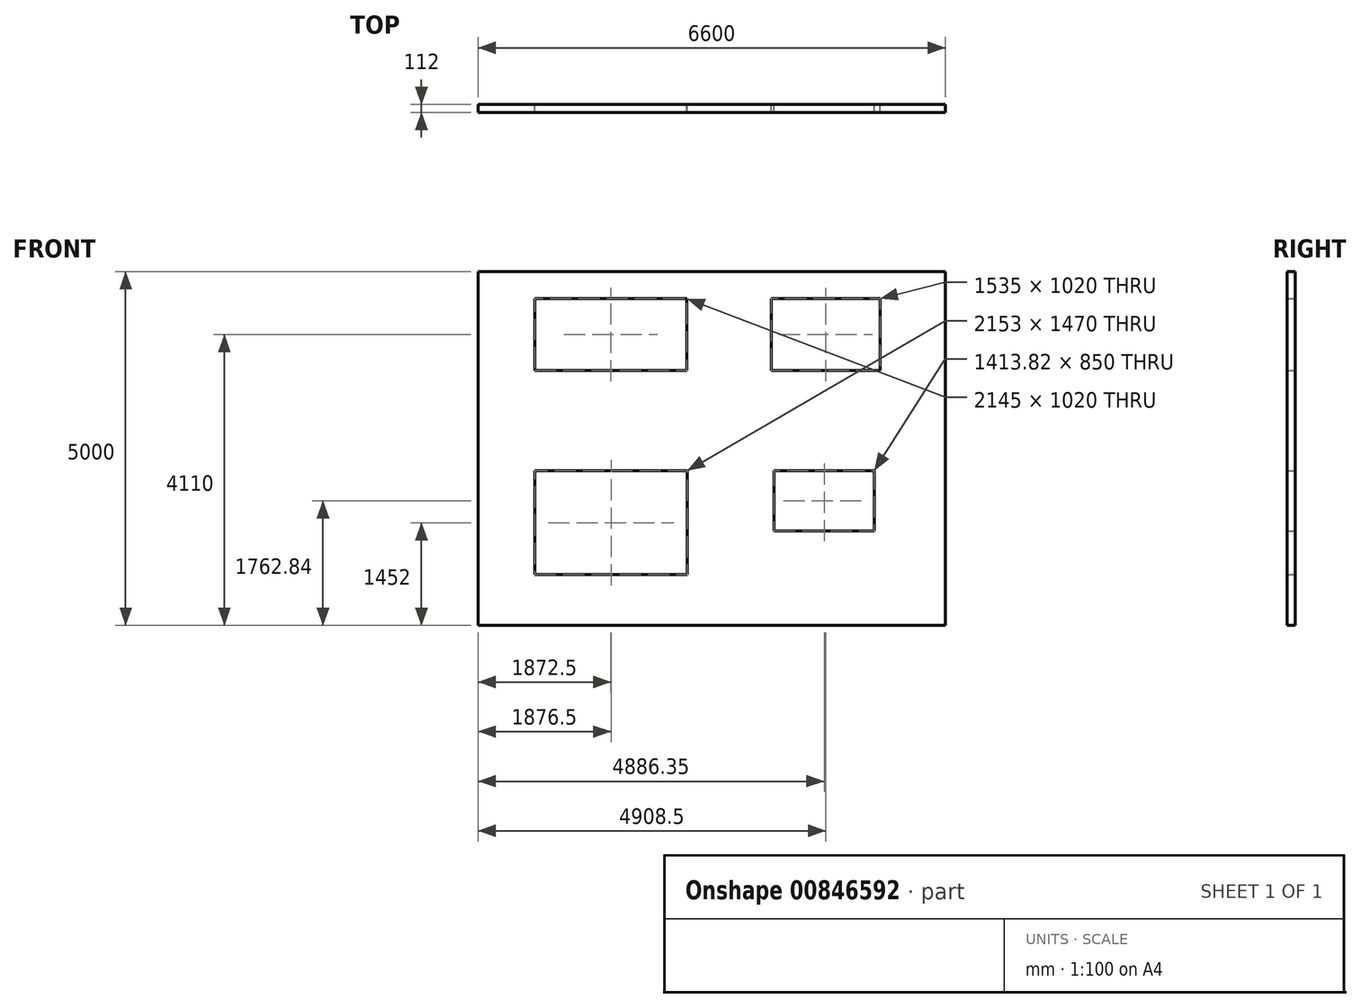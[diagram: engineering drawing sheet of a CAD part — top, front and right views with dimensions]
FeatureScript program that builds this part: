
annotation { "Feature Type Name" : "Feature", "Feature Type Description" : "" }
export const myFeature = defineFeature(function(context is Context, id is Id, definition is map)
    precondition{}
    {
        {
            var Q0;
            Q0=qCreatedBy(makeId("Front.planeOp"),FACE);
            var sketch = newSketch(context, id + "F0", { "sketchPlane" : qUnion([Q0])});
            skLineSegment(sketch, "E0.bottom", {"start": v(3288.8, -2773.48) * mm, "end": v(-3311.2, -2773.48) * mm});
            skLineSegment(sketch, "E0.top", {"start": v(3288.8, 2226.52) * mm, "end": v(-3311.2, 2226.52) * mm});
            skLineSegment(sketch, "E0.left", {"start": v(3288.8, -2773.48) * mm, "end": v(3288.8, 2226.52) * mm});
            skLineSegment(sketch, "E0.right", {"start": v(-3311.2, -2773.48) * mm, "end": v(-3311.2, 2226.52) * mm});
            skLineSegment(sketch, "E1.bottom", {"start": v(-2511.2, 1846.52) * mm, "end": v(-366.2, 1846.52) * mm});
            skLineSegment(sketch, "E1.top", {"start": v(-2511.2, 826.52) * mm, "end": v(-366.2, 826.52) * mm});
            skLineSegment(sketch, "E1.left", {"start": v(-2511.2, 1846.52) * mm, "end": v(-2511.2, 826.52) * mm});
            skLineSegment(sketch, "E1.right", {"start": v(-366.2, 1846.52) * mm, "end": v(-366.2, 826.52) * mm});
            skLineSegment(sketch, "E2.bottom", {"start": v(2364.8, 1846.52) * mm, "end": v(829.8, 1846.52) * mm});
            skLineSegment(sketch, "E2.top", {"start": v(2364.8, 826.52) * mm, "end": v(829.8, 826.52) * mm});
            skLineSegment(sketch, "E2.left", {"start": v(2364.8, 1846.52) * mm, "end": v(2364.8, 826.52) * mm});
            skLineSegment(sketch, "E2.right", {"start": v(829.8, 1846.52) * mm, "end": v(829.8, 826.52) * mm});
            skLineSegment(sketch, "E3.bottom", {"start": v(-2511.2, -2056.48) * mm, "end": v(-358.2, -2056.48) * mm});
            skLineSegment(sketch, "E3.top", {"start": v(-2511.2, -586.48) * mm, "end": v(-358.2, -586.48) * mm});
            skLineSegment(sketch, "E3.left", {"start": v(-2511.2, -2056.48) * mm, "end": v(-2511.2, -586.48) * mm});
            skLineSegment(sketch, "E3.right", {"start": v(-358.2, -2056.48) * mm, "end": v(-358.2, -586.48) * mm});
            skLineSegment(sketch, "E4.bottom", {"start": v(2282.06, -585.64) * mm, "end": v(868.24, -585.64) * mm});
            skLineSegment(sketch, "E4.top", {"start": v(2282.06, -1435.64) * mm, "end": v(868.24, -1435.64) * mm});
            skLineSegment(sketch, "E4.left", {"start": v(2282.06, -585.64) * mm, "end": v(2282.06, -1435.64) * mm});
            skLineSegment(sketch, "E4.right", {"start": v(868.24, -585.64) * mm, "end": v(868.24, -1435.64) * mm});
            skSolve(sketch);
        }
        {
            var Q0;
            Q0 = qSketchRegion(id + "F0", true);
            extrude(context, id + "F1", {"entities" : qUnion([Q0]), "depth" : 112 * mm, "offsetDistance" : 25 * mm});
        }
    });
